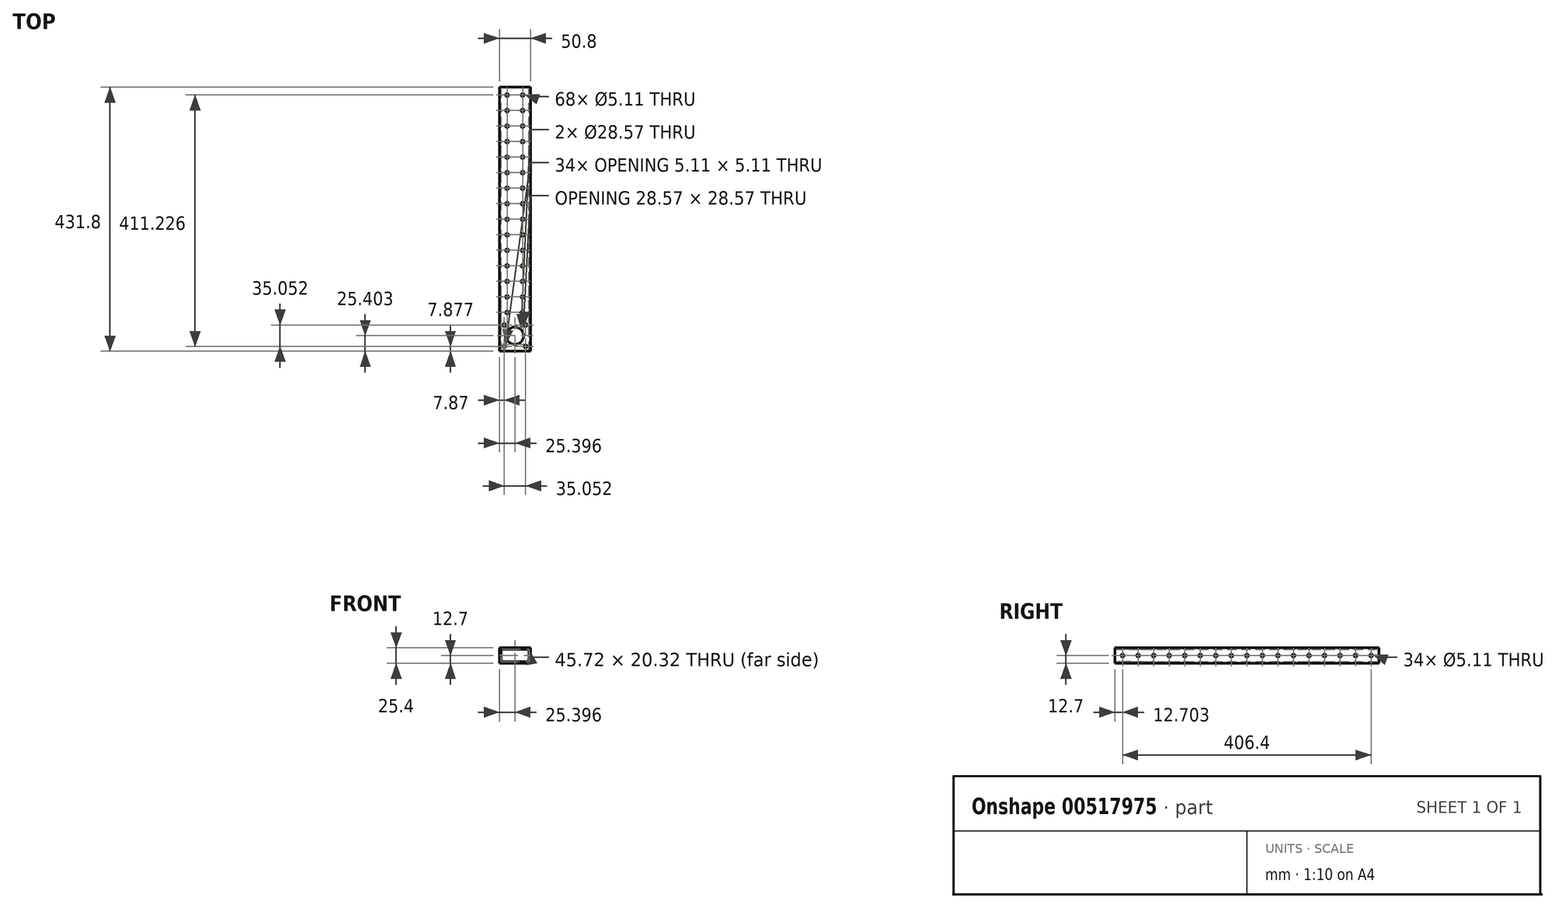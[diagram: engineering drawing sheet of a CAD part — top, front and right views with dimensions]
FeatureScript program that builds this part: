
annotation { "Feature Type Name" : "Feature", "Feature Type Description" : "" }
export const myFeature = defineFeature(function(context is Context, id is Id, definition is map)
    precondition{}
    {
        {
            var Q0;
            Q0=qCreatedBy(makeId("Top.planeOp"),FACE);
            var sketch = newSketch(context, id + "F0", { "sketchPlane" : qUnion([Q0])});
            skLineSegment(sketch, "E0.bottom", {"start": v(-53.5, 445.3) * mm, "end": v(-2.7, 445.3) * mm});
            skLineSegment(sketch, "E0.top", {"start": v(-53.5, 13.5) * mm, "end": v(-2.7, 13.5) * mm});
            skLineSegment(sketch, "E0.left", {"start": v(-53.5, 445.3) * mm, "end": v(-53.5, 13.5) * mm});
            skLineSegment(sketch, "E0.right", {"start": v(-2.7, 445.3) * mm, "end": v(-2.7, 13.5) * mm});
            skSolve(sketch);
        }
        {
            var Q0;
            Q0=makeQuery(id+"F0.imprint","IMPRINT",FACE,{"disambiguationData":[TD([[makeQuery(id+"F0.imprint","IMPRINT",EDGE,{"derivedFrom":sQuery(id+"F0.wireOp",EDGE,"E0.bottom")}),-1.0]])]});
            extrude(context, id + "F1", {"entities" : qUnion([Q0]), "depth" : 25.4 * mm, "offsetDistance" : 25.4 * mm});
        }
        {
            var Q0;
            Q0=makeQuery(id+"F1.opExtrude","SWEPT_FACE",FACE,{"disambiguationData":[OSD([sQuery(id+"F0.wireOp",EDGE,"E0.bottom")])]});
            var sketch = newSketch(context, id + "F2", { "sketchPlane" : qUnion([Q0])});
            skLineSegment(sketch, "E1.bottom", {"start": v(5.24, 22.86) * mm, "end": v(50.96, 22.86) * mm});
            skLineSegment(sketch, "E1.top", {"start": v(5.24, 2.54) * mm, "end": v(50.96, 2.54) * mm});
            skLineSegment(sketch, "E1.left", {"start": v(5.24, 22.86) * mm, "end": v(5.24, 2.54) * mm});
            skLineSegment(sketch, "E1.right", {"start": v(50.96, 22.86) * mm, "end": v(50.96, 2.54) * mm});
            skSolve(sketch);
        }
        {
            var Q0;
            Q0=makeQuery(id+"F1.opExtrude","SWEPT_FACE",FACE,{"disambiguationData":[OSD([sQuery(id+"F0.wireOp",EDGE,"E0.left")])]});
            var sketch = newSketch(context, id + "F3", { "sketchPlane" : qUnion([Q0])});
            skCircle(sketch, "E2", {"center": v(-432.6, 12.7) * mm, "radius": 2.55 * mm});
            skCircle(sketch, "E3.1.0.0", {"center": v(-407.2, 12.7) * mm, "radius": 2.55 * mm});
            skCircle(sketch, "E3.2.0.0", {"center": v(-381.8, 12.7) * mm, "radius": 2.55 * mm});
            skCircle(sketch, "E3.3.0.0", {"center": v(-356.4, 12.7) * mm, "radius": 2.55 * mm});
            skCircle(sketch, "E3.4.0.0", {"center": v(-331, 12.7) * mm, "radius": 2.55 * mm});
            skCircle(sketch, "E3.5.0.0", {"center": v(-305.6, 12.7) * mm, "radius": 2.55 * mm});
            skCircle(sketch, "E3.6.0.0", {"center": v(-280.2, 12.7) * mm, "radius": 2.55 * mm});
            skCircle(sketch, "E3.7.0.0", {"center": v(-254.8, 12.7) * mm, "radius": 2.55 * mm});
            skCircle(sketch, "E3.8.0.0", {"center": v(-229.4, 12.7) * mm, "radius": 2.55 * mm});
            skCircle(sketch, "E3.9.0.0", {"center": v(-204, 12.7) * mm, "radius": 2.55 * mm});
            skCircle(sketch, "E3.10.0.0", {"center": v(-178.6, 12.7) * mm, "radius": 2.55 * mm});
            skCircle(sketch, "E3.11.0.0", {"center": v(-153.2, 12.7) * mm, "radius": 2.55 * mm});
            skCircle(sketch, "E3.12.0.0", {"center": v(-127.8, 12.7) * mm, "radius": 2.55 * mm});
            skCircle(sketch, "E3.13.0.0", {"center": v(-102.4, 12.7) * mm, "radius": 2.55 * mm});
            skCircle(sketch, "E3.14.0.0", {"center": v(-77, 12.7) * mm, "radius": 2.55 * mm});
            skCircle(sketch, "E3.15.0.0", {"center": v(-51.6, 12.7) * mm, "radius": 2.55 * mm});
            skCircle(sketch, "E3.16.0.0", {"center": v(-26.2, 12.7) * mm, "radius": 2.55 * mm});
            skLineSegment(sketch, "E3.direction1", {"start": v(-432.6, 12.7) * mm, "end": v(-407.2, 12.7) * mm, "construction": true});
            skSolve(sketch);
        }
        {
            var Q0;
            Q0=sQuery(id+"F3.wireOp",VERTEX,"E3.16.0.0.center");
            var Q1;
            Q1=sQuery(id+"F3.wireOp",VERTEX,"E3.4.0.0.center");
            var Q2;
            Q2=sQuery(id+"F3.wireOp",VERTEX,"E3.2.0.0.center");
            var Q3;
            Q3=sQuery(id+"F3.wireOp",VERTEX,"E3.3.0.0.center");
            var Q4;
            Q4=sQuery(id+"F3.wireOp",VERTEX,"E3.1.0.0.center");
            var Q5;
            Q5=sQuery(id+"F3.wireOp",VERTEX,"E3.10.0.0.center");
            var Q6;
            Q6=sQuery(id+"F3.wireOp",VERTEX,"E3.8.0.0.center");
            var Q7;
            Q7=sQuery(id+"F3.wireOp",VERTEX,"E3.9.0.0.center");
            var Q8;
            Q8=sQuery(id+"F3.wireOp",VERTEX,"E3.6.0.0.center");
            var Q9;
            Q9=sQuery(id+"F3.wireOp",VERTEX,"E3.7.0.0.center");
            var Q10;
            Q10=sQuery(id+"F3.wireOp",VERTEX,"E3.5.0.0.center");
            var Q11;
            Q11=sQuery(id+"F3.wireOp",VERTEX,"E3.13.0.0.center");
            var Q12;
            Q12=sQuery(id+"F3.wireOp",VERTEX,"E3.11.0.0.center");
            var Q13;
            Q13=sQuery(id+"F3.wireOp",VERTEX,"E3.15.0.0.center");
            var Q14;
            Q14=sQuery(id+"F3.wireOp",VERTEX,"E3.12.0.0.center");
            var Q15;
            Q15=sQuery(id+"F3.wireOp",VERTEX,"E3.14.0.0.center");
            var Q16;
            Q16=sQuery(id+"F3.wireOp",VERTEX,"E3.direction1.start");
            var Q17;
            Q17=makeQuery(id+"F1.opExtrude","SWEPT_BODY",BODY,{"disambiguationData":[OSD([sQuery(id+"F0.wireOp",EDGE,"E0.bottom"),sQuery(id+"F0.wireOp",EDGE,"E0.top"),sQuery(id+"F0.wireOp",EDGE,"E0.left"),sQuery(id+"F0.wireOp",EDGE,"E0.right")])]});
            hole(context, id + "F4", {"style" : HoleStyle.SIMPLE, "endStyle" : HoleEndStyle.THROUGH, "holeDiameter" : 5.1 * mm, "isTappedThrough" : true, "tappedDepth" : 12.7 * mm, "tapClearance" : 3, "locations" : qUnion([Q0, Q1, Q2, Q3, Q4, Q5, Q6, Q7, Q8, Q9, Q10, Q11, Q12, Q13, Q14, Q15, Q16]), "scope" : qUnion([Q17])});
        }
        {
            var Q0;
            Q0=makeQuery(id+"F1.opExtrude","CAP_FACE",FACE,{"disambiguationData":[OSD([sQuery(id+"F0.wireOp",EDGE,"E0.bottom"),sQuery(id+"F0.wireOp",EDGE,"E0.top"),sQuery(id+"F0.wireOp",EDGE,"E0.left"),sQuery(id+"F0.wireOp",EDGE,"E0.right")])],"isStart":false});
            var sketch = newSketch(context, id + "F5", { "sketchPlane" : qUnion([Q0])});
            skCircle(sketch, "E4", {"center": v(-40.8, 432.6) * mm, "radius": 2.55 * mm});
            skCircle(sketch, "E5.0.1.0", {"center": v(-40.8, 407.2) * mm, "radius": 2.55 * mm});
            skCircle(sketch, "E5.0.2.0", {"center": v(-40.8, 381.8) * mm, "radius": 2.55 * mm});
            skCircle(sketch, "E5.0.3.0", {"center": v(-40.8, 356.4) * mm, "radius": 2.55 * mm});
            skCircle(sketch, "E5.0.4.0", {"center": v(-40.8, 331) * mm, "radius": 2.55 * mm});
            skCircle(sketch, "E5.0.5.0", {"center": v(-40.8, 305.6) * mm, "radius": 2.55 * mm});
            skCircle(sketch, "E5.0.6.0", {"center": v(-40.8, 280.2) * mm, "radius": 2.55 * mm});
            skCircle(sketch, "E5.0.7.0", {"center": v(-40.8, 254.8) * mm, "radius": 2.55 * mm});
            skCircle(sketch, "E5.0.8.0", {"center": v(-40.8, 229.4) * mm, "radius": 2.55 * mm});
            skCircle(sketch, "E5.0.9.0", {"center": v(-40.8, 204) * mm, "radius": 2.55 * mm});
            skCircle(sketch, "E5.0.10.0", {"center": v(-40.8, 178.6) * mm, "radius": 2.55 * mm});
            skCircle(sketch, "E5.0.11.0", {"center": v(-40.8, 153.2) * mm, "radius": 2.55 * mm});
            skCircle(sketch, "E5.0.12.0", {"center": v(-40.8, 127.8) * mm, "radius": 2.55 * mm});
            skCircle(sketch, "E5.0.13.0", {"center": v(-40.8, 102.4) * mm, "radius": 2.55 * mm});
            skCircle(sketch, "E5.0.14.0", {"center": v(-40.8, 77) * mm, "radius": 2.55 * mm});
            skCircle(sketch, "E5.1.0.0", {"center": v(-15.4, 432.6) * mm, "radius": 2.55 * mm});
            skCircle(sketch, "E5.1.1.0", {"center": v(-15.4, 407.2) * mm, "radius": 2.55 * mm});
            skCircle(sketch, "E5.1.2.0", {"center": v(-15.4, 381.8) * mm, "radius": 2.55 * mm});
            skCircle(sketch, "E5.1.3.0", {"center": v(-15.4, 356.4) * mm, "radius": 2.55 * mm});
            skCircle(sketch, "E5.1.4.0", {"center": v(-15.4, 331) * mm, "radius": 2.55 * mm});
            skCircle(sketch, "E5.1.5.0", {"center": v(-15.4, 305.6) * mm, "radius": 2.55 * mm});
            skCircle(sketch, "E5.1.6.0", {"center": v(-15.4, 280.2) * mm, "radius": 2.55 * mm});
            skCircle(sketch, "E5.1.7.0", {"center": v(-15.4, 254.8) * mm, "radius": 2.55 * mm});
            skCircle(sketch, "E5.1.8.0", {"center": v(-15.4, 229.4) * mm, "radius": 2.55 * mm});
            skCircle(sketch, "E5.1.9.0", {"center": v(-15.4, 204) * mm, "radius": 2.55 * mm});
            skCircle(sketch, "E5.1.10.0", {"center": v(-15.4, 178.6) * mm, "radius": 2.55 * mm});
            skCircle(sketch, "E5.1.11.0", {"center": v(-15.4, 153.2) * mm, "radius": 2.55 * mm});
            skCircle(sketch, "E5.1.12.0", {"center": v(-15.4, 127.8) * mm, "radius": 2.55 * mm});
            skCircle(sketch, "E5.1.13.0", {"center": v(-15.4, 102.4) * mm, "radius": 2.55 * mm});
            skCircle(sketch, "E5.1.14.0", {"center": v(-15.4, 77) * mm, "radius": 2.55 * mm});
            skLineSegment(sketch, "E5.direction1", {"start": v(-40.8, 432.6) * mm, "end": v(-15.4, 432.6) * mm, "construction": true});
            skLineSegment(sketch, "E5.direction2", {"start": v(-40.8, 432.6) * mm, "end": v(-40.8, 407.2) * mm, "construction": true});
            skSolve(sketch);
        }
        {
            var Q0;
            Q0=sQuery(id+"F5.wireOp",VERTEX,"E5.direction1.start");
            var Q1;
            Q1=sQuery(id+"F5.wireOp",VERTEX,"E5.direction1.end");
            var Q2;
            Q2=sQuery(id+"F5.wireOp",VERTEX,"E5.0.3.0.center");
            var Q3;
            Q3=sQuery(id+"F5.wireOp",VERTEX,"E5.0.2.0.center");
            var Q4;
            Q4=sQuery(id+"F5.wireOp",VERTEX,"E5.0.1.0.center");
            var Q5;
            Q5=sQuery(id+"F5.wireOp",VERTEX,"E5.0.7.0.center");
            var Q6;
            Q6=sQuery(id+"F5.wireOp",VERTEX,"E5.1.3.0.center");
            var Q7;
            Q7=sQuery(id+"F5.wireOp",VERTEX,"E5.1.7.0.center");
            var Q8;
            Q8=sQuery(id+"F5.wireOp",VERTEX,"E5.1.12.0.center");
            var Q9;
            Q9=sQuery(id+"F5.wireOp",VERTEX,"E5.0.13.0.center");
            var Q10;
            Q10=sQuery(id+"F5.wireOp",VERTEX,"E5.1.1.0.center");
            var Q11;
            Q11=sQuery(id+"F5.wireOp",VERTEX,"E5.1.4.0.center");
            var Q12;
            Q12=sQuery(id+"F5.wireOp",VERTEX,"E5.1.5.0.center");
            var Q13;
            Q13=sQuery(id+"F5.wireOp",VERTEX,"E5.0.9.0.center");
            var Q14;
            Q14=sQuery(id+"F5.wireOp",VERTEX,"E5.0.5.0.center");
            var Q15;
            Q15=sQuery(id+"F5.wireOp",VERTEX,"E5.1.6.0.center");
            var Q16;
            Q16=sQuery(id+"F5.wireOp",VERTEX,"E5.1.16.0.center");
            var Q17;
            Q17=sQuery(id+"F5.wireOp",VERTEX,"E5.0.12.0.center");
            var Q18;
            Q18=sQuery(id+"F5.wireOp",VERTEX,"E5.1.2.0.center");
            var Q19;
            Q19=sQuery(id+"F5.wireOp",VERTEX,"E5.0.16.0.center");
            var Q20;
            Q20=sQuery(id+"F5.wireOp",VERTEX,"E5.0.14.0.center");
            var Q21;
            Q21=sQuery(id+"F5.wireOp",VERTEX,"E5.0.10.0.center");
            var Q22;
            Q22=sQuery(id+"F5.wireOp",VERTEX,"E5.0.6.0.center");
            var Q23;
            Q23=sQuery(id+"F5.wireOp",VERTEX,"E5.1.14.0.center");
            var Q24;
            Q24=sQuery(id+"F5.wireOp",VERTEX,"E5.1.9.0.center");
            var Q25;
            Q25=sQuery(id+"F5.wireOp",VERTEX,"E5.1.10.0.center");
            var Q26;
            Q26=sQuery(id+"F5.wireOp",VERTEX,"E5.1.15.0.center");
            var Q27;
            Q27=sQuery(id+"F5.wireOp",VERTEX,"E5.1.8.0.center");
            var Q28;
            Q28=sQuery(id+"F5.wireOp",VERTEX,"E5.1.11.0.center");
            var Q29;
            Q29=sQuery(id+"F5.wireOp",VERTEX,"E5.0.4.0.center");
            var Q30;
            Q30=sQuery(id+"F5.wireOp",VERTEX,"E5.0.8.0.center");
            var Q31;
            Q31=sQuery(id+"F5.wireOp",VERTEX,"E5.0.15.0.center");
            var Q32;
            Q32=sQuery(id+"F5.wireOp",VERTEX,"E5.1.13.0.center");
            var Q33;
            Q33=sQuery(id+"F5.wireOp",VERTEX,"E5.0.11.0.center");
            var Q34;
            Q34=makeQuery(id+"F1.opExtrude","SWEPT_BODY",BODY,{"disambiguationData":[OSD([sQuery(id+"F0.wireOp",EDGE,"E0.bottom"),sQuery(id+"F0.wireOp",EDGE,"E0.top"),sQuery(id+"F0.wireOp",EDGE,"E0.left"),sQuery(id+"F0.wireOp",EDGE,"E0.right")])]});
            hole(context, id + "F6", {"style" : HoleStyle.SIMPLE, "endStyle" : HoleEndStyle.THROUGH, "holeDiameter" : 5.1 * mm, "isTappedThrough" : true, "tappedDepth" : 12.7 * mm, "tapClearance" : 3, "locations" : qUnion([Q0, Q1, Q2, Q3, Q4, Q5, Q6, Q7, Q8, Q9, Q10, Q11, Q12, Q13, Q14, Q15, Q16, Q17, Q18, Q19, Q20, Q21, Q22, Q23, Q24, Q25, Q26, Q27, Q28, Q29, Q30, Q31, Q32, Q33]), "scope" : qUnion([Q34])});
        }
        {
            var Q0;
            Q0=makeQuery(id+"F1.opExtrude","CAP_FACE",FACE,{"disambiguationData":[OSD([sQuery(id+"F0.wireOp",EDGE,"E0.bottom"),sQuery(id+"F0.wireOp",EDGE,"E0.top"),sQuery(id+"F0.wireOp",EDGE,"E0.left"),sQuery(id+"F0.wireOp",EDGE,"E0.right")])],"isStart":false});
            var sketch = newSketch(context, id + "F7", { "sketchPlane" : qUnion([Q0])});
            skCircle(sketch, "E6", {"center": v(-28.1, 38.9) * mm, "radius": 14.29 * mm});
            skLineSegment(sketch, "E7.bottom", {"start": v(-45.63, 56.43) * mm, "end": v(-10.58, 56.43) * mm});
            skLineSegment(sketch, "E7.top", {"start": v(-45.63, 21.38) * mm, "end": v(-10.58, 21.38) * mm});
            skLineSegment(sketch, "E7.left", {"start": v(-45.63, 56.43) * mm, "end": v(-45.63, 21.38) * mm});
            skLineSegment(sketch, "E7.right", {"start": v(-10.58, 56.43) * mm, "end": v(-10.58, 21.38) * mm});
            skCircle(sketch, "E8", {"center": v(-45.63, 56.43) * mm, "radius": 2.55 * mm});
            skCircle(sketch, "E9", {"center": v(-10.58, 56.43) * mm, "radius": 2.55 * mm});
            skCircle(sketch, "E10", {"center": v(-45.63, 21.38) * mm, "radius": 2.55 * mm});
            skCircle(sketch, "E11", {"center": v(-10.58, 21.38) * mm, "radius": 2.55 * mm});
            skSolve(sketch);
        }
        {
            var Q0;
            Q0=sQuery(id+"F7.wireOp",VERTEX,"E7.bottom.start");
            var Q1;
            Q1=sQuery(id+"F7.wireOp",VERTEX,"E9.center");
            var Q2;
            Q2=sQuery(id+"F7.wireOp",VERTEX,"E7.right.end");
            var Q3;
            Q3=sQuery(id+"F7.wireOp",VERTEX,"E10.center");
            var Q4;
            Q4=makeQuery(id+"F1.opExtrude","SWEPT_BODY",BODY,{"disambiguationData":[OSD([sQuery(id+"F0.wireOp",EDGE,"E0.bottom"),sQuery(id+"F0.wireOp",EDGE,"E0.top"),sQuery(id+"F0.wireOp",EDGE,"E0.left"),sQuery(id+"F0.wireOp",EDGE,"E0.right")])]});
            hole(context, id + "F8", {"style" : HoleStyle.SIMPLE, "endStyle" : HoleEndStyle.THROUGH, "holeDiameter" : 5.1 * mm, "isTappedThrough" : true, "tappedDepth" : 12.7 * mm, "tapClearance" : 3, "locations" : qUnion([Q0, Q1, Q2, Q3]), "scope" : qUnion([Q4])});
        }
        {
            var Q0;
            Q0=makeQuery(id+"F2.imprint","IMPRINT",FACE,{"disambiguationData":[TD([[makeQuery(id+"F2.imprint","IMPRINT",EDGE,{"derivedFrom":sQuery(id+"F2.wireOp",EDGE,"E1.bottom")}),-1.0]])]});
            extrude(context, id + "F9", {"entities" : qUnion([Q0]), "operationType" : NewBodyOperationType.REMOVE, "oppositeDirection" : true, "depth" : 431.8 * mm, "offsetDistance" : 25.4 * mm});
        }
        {
            var Q0;
            Q0=sQuery(id+"F7.wireOp",VERTEX,"E6.center");
            var Q1;
            Q1=makeQuery(id+"F1.opExtrude","SWEPT_BODY",BODY,{"disambiguationData":[OSD([sQuery(id+"F0.wireOp",EDGE,"E0.bottom"),sQuery(id+"F0.wireOp",EDGE,"E0.top"),sQuery(id+"F0.wireOp",EDGE,"E0.left"),sQuery(id+"F0.wireOp",EDGE,"E0.right")])]});
            hole(context, id + "F10", {"style" : HoleStyle.SIMPLE, "endStyle" : HoleEndStyle.THROUGH, "holeDiameter" : 28.57 * mm, "isTappedThrough" : true, "tappedDepth" : 12.7 * mm, "tapClearance" : 3, "locations" : qUnion([Q0]), "scope" : qUnion([Q1])});
        }
    });
